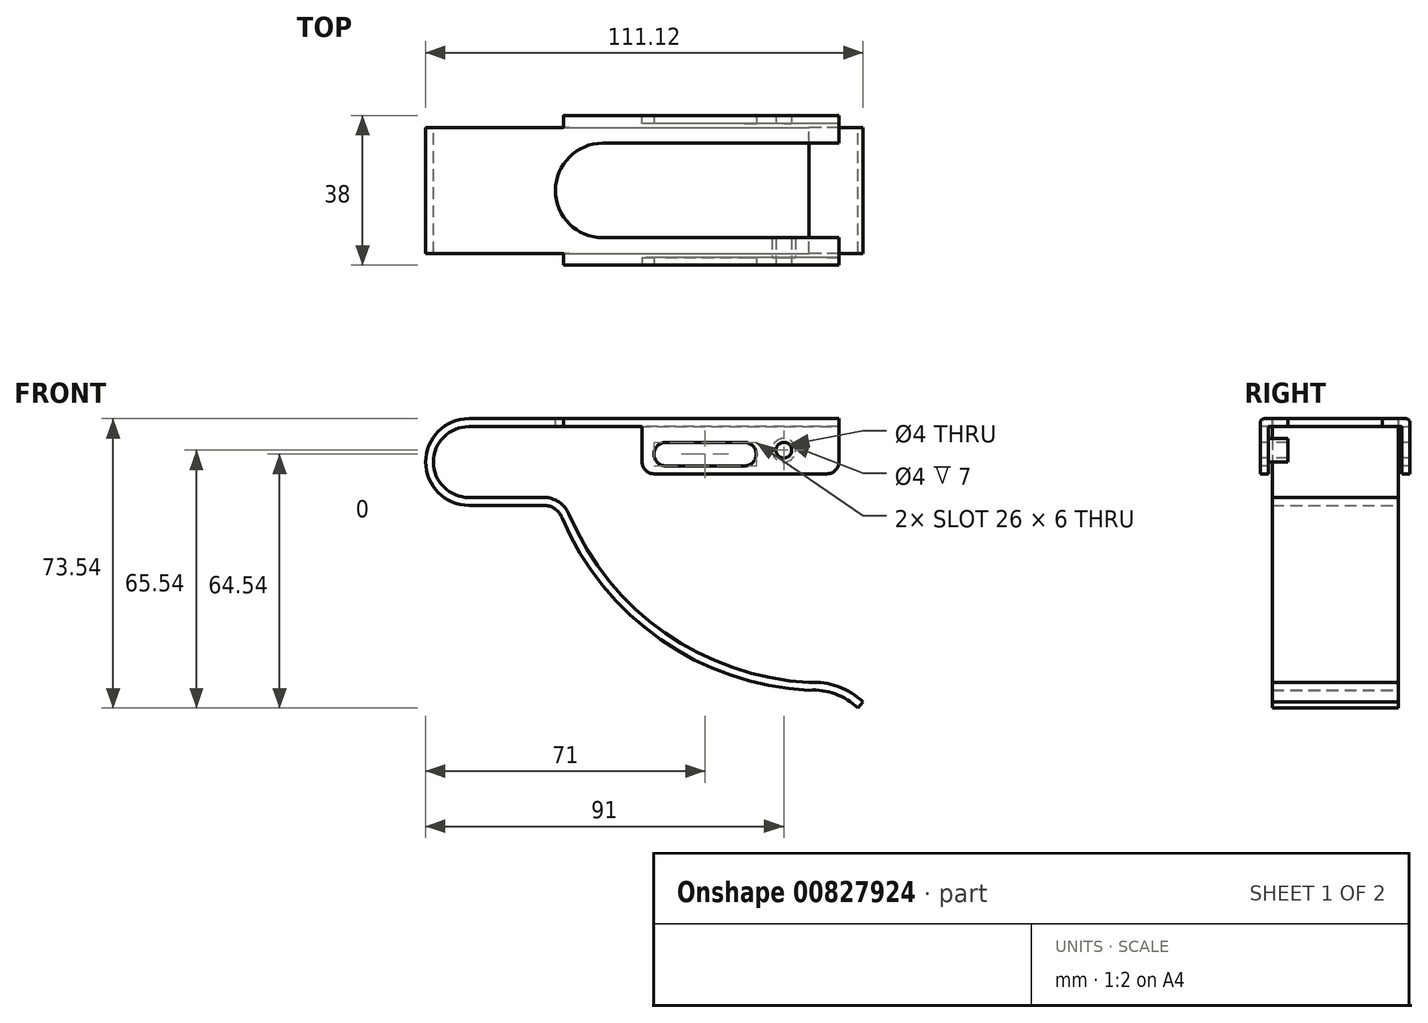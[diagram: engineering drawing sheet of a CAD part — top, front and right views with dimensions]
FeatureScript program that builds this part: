
annotation { "Feature Type Name" : "Feature", "Feature Type Description" : "" }
export const myFeature = defineFeature(function(context is Context, id is Id, definition is map)
    precondition{}
    {
        {
            var Q0;
            Q0=qCreatedBy(makeId("Front.planeOp"),FACE);
            var sketch = newSketch(context, id + "F0", { "sketchPlane" : qUnion([Q0])});
            skArc(sketch, "E0", {"start": v(0, 11) * mm, "mid": v(-11, 0) * mm, "end": v(0, -11) * mm});
            skLineSegment(sketch, "E1", {"start": v(0, 11) * mm, "end": v(94, 11) * mm});
            skLineSegment(sketch, "E2", {"start": v(0, -11) * mm, "end": v(19, -11) * mm});
            skArc(sketch, "E3", {"start": v(23.6, -14.06) * mm, "mid": v(48.7, -45.1) * mm, "end": v(86.45, -58) * mm});
            skArc(sketch, "E4", {"start": v(98.83, -62.54) * mm, "mid": v(93.13, -58.94) * mm, "end": v(86.45, -58) * mm});
            skPoint(sketch, "E5.visualSharp", {"position": v(22.4, -11) * mm});
            skArc(sketch, "E5.filletArc", {"start": v(23.6, -14.06) * mm, "mid": v(21.76, -11.83) * mm, "end": v(19, -11) * mm});
            skLineSegment(sketch, "E6.0", {"start": v(0, 9) * mm, "end": v(94, 9) * mm});
            skArc(sketch, "E6.1", {"start": v(0, 9) * mm, "mid": v(-9, 0) * mm, "end": v(0, -9) * mm});
            skArc(sketch, "E6.2", {"start": v(100.12, -61) * mm, "mid": v(93.8, -57.05) * mm, "end": v(86.43, -56) * mm});
            skArc(sketch, "E6.3", {"start": v(25.45, -13.28) * mm, "mid": v(49.79, -43.42) * mm, "end": v(86.43, -56) * mm});
            skArc(sketch, "E6.4", {"start": v(25.45, -13.28) * mm, "mid": v(22.87, -10.17) * mm, "end": v(19, -9) * mm});
            skLineSegment(sketch, "E6.5", {"start": v(0, -9) * mm, "end": v(19, -9) * mm});
            skLineSegment(sketch, "E7", {"start": v(94, 11) * mm, "end": v(94, 9) * mm});
            skLineSegment(sketch, "E8", {"start": v(100.12, -61) * mm, "end": v(98.83, -62.54) * mm});
            skLineSegment(sketch, "E9", {"start": v(100.12, -61) * mm, "end": v(153.54, -61) * mm});
            skSolve(sketch);
        }
        {
            var Q0;
            Q0=qSketchRegion(id+"F0",true);
            extrude(context, id + "F1", {"entities" : qUnion([Q0]), "depth" : 16 * mm, "offsetDistance" : 25 * mm});
        }
        {
            var Q0;
            Q0=makeQuery(id+"F1.opExtrude","SWEPT_FACE",FACE,{"disambiguationData":[OSD([sQuery(id+"F0.wireOp",EDGE,"E1")])]});
            var sketch = newSketch(context, id + "F2", { "sketchPlane" : qUnion([Q0])});
            skLineSegment(sketch, "E10.bottom", {"start": v(94, -16) * mm, "end": v(24, -16) * mm});
            skLineSegment(sketch, "E10.top", {"start": v(94, -19) * mm, "end": v(24, -19) * mm});
            skLineSegment(sketch, "E10.left", {"start": v(94, -16) * mm, "end": v(94, -19) * mm});
            skLineSegment(sketch, "E10.right", {"start": v(24, -16) * mm, "end": v(24, -19) * mm});
            skSolve(sketch);
        }
        {
            var Q0;
            Q0=makeQuery(id+"F2.imprint","IMPRINT",FACE,{"disambiguationData":[TD([[makeQuery(id+"F2.imprint","IMPRINT",EDGE,{"derivedFrom":sQuery(id+"F2.wireOp",EDGE,"E10.bottom")}),-1.0]])]});
            extrude(context, id + "F3", {"entities" : qUnion([Q0]), "operationType" : NewBodyOperationType.ADD, "oppositeDirection" : true, "depth" : 2 * mm, "offsetDistance" : 25 * mm});
        }
        {
            var Q0;
            Q0=makeQuery(id+"F3.opExtrude","SWEPT_FACE",FACE,{"disambiguationData":[OSD([sQuery(id+"F2.wireOp",EDGE,"E10.top")])]});
            var sketch = newSketch(context, id + "F4", { "sketchPlane" : qUnion([Q0])});
            skLineSegment(sketch, "E11.bottom", {"start": v(94, 11) * mm, "end": v(44, 11) * mm});
            skLineSegment(sketch, "E11.top", {"start": v(94, -3) * mm, "end": v(44, -3) * mm});
            skLineSegment(sketch, "E11.left", {"start": v(94, 11) * mm, "end": v(94, -3) * mm});
            skLineSegment(sketch, "E11.right", {"start": v(44, 11) * mm, "end": v(44, -3) * mm});
            skSolve(sketch);
        }
        {
            var Q0;
            {var subQ0=sQuery(id+"F4.wireOp",EDGE,"E11.top");Q0=makeQuery(id+"F4.imprint","IMPRINT",FACE,{"disambiguationData":[TD([[makeQuery(id+"F4.imprint","IMPRINT",EDGE,{"derivedFrom":subQ0}),-1.0]])]});}
            extrude(context, id + "F5", {"entities" : qUnion([Q0]), "operationType" : NewBodyOperationType.ADD, "oppositeDirection" : true, "depth" : 2 * mm, "offsetDistance" : 25 * mm});
        }
        {
            var Q0;
            Q0=makeQuery(id+"F3.opExtrude","CAP_EDGE",EDGE,{"disambiguationData":[OSD([sQuery(id+"F2.wireOp",EDGE,"E10.top")])],"isStart":true});
            var Q1;
            Q1=makeQuery(id+"F5.opExtrude","CAP_EDGE",EDGE,{"disambiguationData":[OSD([sQuery(id+"F2.wireOp",EDGE,"E10.top")])],"isStart":false});
            fillet(context, id + "F6", {"entities" : qUnion([Q0, Q1]), "radius" : 1 * mm, "allowEdgeOverflow" : false});
        }
        {
            var Q0;
            Q0=makeQuery(id+"F1.opExtrude","SWEPT_BODY",BODY,{"disambiguationData":[OSD([sQuery(id+"F0.wireOp",EDGE,"E0"),sQuery(id+"F0.wireOp",EDGE,"E1"),sQuery(id+"F0.wireOp",EDGE,"E2"),sQuery(id+"F0.wireOp",EDGE,"E3"),sQuery(id+"F0.wireOp",EDGE,"E4"),sQuery(id+"F0.wireOp",EDGE,"E5.filletArc"),sQuery(id+"F0.wireOp",EDGE,"E6.0"),sQuery(id+"F0.wireOp",EDGE,"E6.1"),sQuery(id+"F0.wireOp",EDGE,"E6.2"),sQuery(id+"F0.wireOp",EDGE,"E6.3"),sQuery(id+"F0.wireOp",EDGE,"E6.4"),sQuery(id+"F0.wireOp",EDGE,"E6.5"),sQuery(id+"F0.wireOp",EDGE,"E7"),sQuery(id+"F0.wireOp",EDGE,"E8")])]});
            var Q1;
            Q1=qCreatedBy(makeId("Front.planeOp"),FACE);
            mirror(context, id + "F7", {"operationType" : NewBodyOperationType.ADD, "entities" : qUnion([Q0]), "mirrorPlane" : qUnion([Q1])});
        }
        {
            var Q0;
            {var subQ0=makeQuery(id+"F3.boolean.opBoolean","MERGE",FACE,{"derivedFrom":[makeQuery(id+"F1.opExtrude","SWEPT_FACE",FACE,{"disambiguationData":[OSD([sQuery(id+"F0.wireOp",EDGE,"E1")])]}),makeQuery(id+"F3.opExtrude","CAP_FACE",FACE,{"disambiguationData":[OSD([sQuery(id+"F2.wireOp",EDGE,"E10.bottom"),sQuery(id+"F2.wireOp",EDGE,"E10.top"),sQuery(id+"F2.wireOp",EDGE,"E10.left"),sQuery(id+"F2.wireOp",EDGE,"E10.right")])],"isStart":true})]});Q0=makeQuery(id+"F7.boolean.opBoolean","MERGE",FACE,{"derivedFrom":[subQ0,makeQuery(id+"F7.opPattern","COPY",FACE,{"derivedFrom":subQ0,"instanceName":"1"})]});}
            var sketch = newSketch(context, id + "F8", { "sketchPlane" : qUnion([Q0])});
            skLineSegment(sketch, "E12", {"start": v(34, 12) * mm, "end": v(94, 12) * mm});
            skLineSegment(sketch, "E13", {"start": v(34, -12) * mm, "end": v(94, -12) * mm});
            skLineSegment(sketch, "E14", {"start": v(94, -12) * mm, "end": v(94, 12) * mm});
            skPoint(sketch, "E15.center.orphan", {"position": v(34, 0) * mm});
            skArc(sketch, "E16", {"start": v(34, 12) * mm, "mid": v(22, 0) * mm, "end": v(34, -12) * mm});
            skSolve(sketch);
        }
        {
            var Q0;
            Q0=qSketchRegion(id+"F8",true);
            extrude(context, id + "F9", {"entities" : qUnion([Q0]), "operationType" : NewBodyOperationType.REMOVE, "oppositeDirection" : true, "depth" : 2 * mm, "offsetDistance" : 25 * mm});
        }
        {
            var Q0;
            {var subQ0=sQuery(id+"F2.wireOp",EDGE,"E10.top");Q0=makeQuery(id+"F5.boolean.opBoolean","MERGE",FACE,{"derivedFrom":[makeQuery(id+"F3.opExtrude","SWEPT_FACE",FACE,{"disambiguationData":[OSD([subQ0])]}),makeQuery(id+"F5.opExtrude","CAP_FACE",FACE,{"disambiguationData":[OSD([subQ0,sQuery(id+"F4.wireOp",EDGE,"E11.top"),sQuery(id+"F4.wireOp",EDGE,"E11.left"),sQuery(id+"F4.wireOp",EDGE,"E11.right")])],"isStart":true})]});}
            var sketch = newSketch(context, id + "F10", { "sketchPlane" : qUnion([Q0])});
            skLineSegment(sketch, "E17", {"start": v(50, 2) * mm, "end": v(70, 2) * mm});
            skLineSegment(sketch, "E18.0", {"start": v(50, -1) * mm, "end": v(70, -1) * mm});
            skLineSegment(sketch, "E19.0", {"start": v(50, 5) * mm, "end": v(70, 5) * mm});
            skArc(sketch, "E20", {"start": v(50, 5) * mm, "mid": v(47, 2) * mm, "end": v(50, -1) * mm});
            skArc(sketch, "E21", {"start": v(70, -1) * mm, "mid": v(73, 2) * mm, "end": v(70, 5) * mm});
            skSolve(sketch);
        }
        {
            var Q0;
            Q0=qSketchRegion(id+"F10",true);
            extrude(context, id + "F11", {"entities" : qUnion([Q0]), "operationType" : NewBodyOperationType.REMOVE, "endBound" : BoundingType.THROUGH_ALL, "oppositeDirection" : true, "depth" : 25 * mm, "offsetDistance" : 25 * mm});
        }
        {
            var Q0;
            {var subQ0=sQuery(id+"F2.wireOp",EDGE,"E10.top");Q0=makeQuery(id+"F5.boolean.opBoolean","MERGE",FACE,{"derivedFrom":[makeQuery(id+"F3.opExtrude","SWEPT_FACE",FACE,{"disambiguationData":[OSD([subQ0])]}),makeQuery(id+"F5.opExtrude","CAP_FACE",FACE,{"disambiguationData":[OSD([subQ0,sQuery(id+"F4.wireOp",EDGE,"E11.top"),sQuery(id+"F4.wireOp",EDGE,"E11.left"),sQuery(id+"F4.wireOp",EDGE,"E11.right")])],"isStart":true})]});}
            var sketch = newSketch(context, id + "F12", { "sketchPlane" : qUnion([Q0])});
            skPoint(sketch, "E22", {"position": v(80, 3) * mm});
            skSolve(sketch);
        }
        {
            var Q0;
            Q0=sQuery(id+"F12.wireOp",VERTEX,"E22");
            var Q1;
            Q1=makeQuery(id+"F1.opExtrude","SWEPT_BODY",BODY,{"disambiguationData":[OSD([sQuery(id+"F0.wireOp",EDGE,"E0"),sQuery(id+"F0.wireOp",EDGE,"E1"),sQuery(id+"F0.wireOp",EDGE,"E2"),sQuery(id+"F0.wireOp",EDGE,"E3"),sQuery(id+"F0.wireOp",EDGE,"E4"),sQuery(id+"F0.wireOp",EDGE,"E5.filletArc"),sQuery(id+"F0.wireOp",EDGE,"E6.0"),sQuery(id+"F0.wireOp",EDGE,"E6.1"),sQuery(id+"F0.wireOp",EDGE,"E6.2"),sQuery(id+"F0.wireOp",EDGE,"E6.3"),sQuery(id+"F0.wireOp",EDGE,"E6.4"),sQuery(id+"F0.wireOp",EDGE,"E6.5"),sQuery(id+"F0.wireOp",EDGE,"E7"),sQuery(id+"F0.wireOp",EDGE,"E8")])]});
            hole(context, id + "F13", {"style" : HoleStyle.SIMPLE, "endStyle" : HoleEndStyle.THROUGH, "holeDiameter" : 4 * mm, "majorDiameter" : 5 * mm, "isTappedThrough" : true, "tappedDepth" : 12 * mm, "tapClearance" : 3, "locations" : qUnion([Q0]), "scope" : qUnion([Q1])});
        }
        {
            var Q0;
            Q0=makeQuery(id+"F5.opExtrude","CAP_FACE",FACE,{"disambiguationData":[OSD([sQuery(id+"F2.wireOp",EDGE,"E10.top"),sQuery(id+"F4.wireOp",EDGE,"E11.top"),sQuery(id+"F4.wireOp",EDGE,"E11.left"),sQuery(id+"F4.wireOp",EDGE,"E11.right")])],"isStart":false});
            var sketch = newSketch(context, id + "F14", { "sketchPlane" : qUnion([Q0])});
            skCircle(sketch, "E23.0", {"center": v(-80, 3) * mm, "radius": 2 * mm});
            skCircle(sketch, "E24.0", {"center": v(-80, 3) * mm, "radius": 3 * mm});
            skSolve(sketch);
        }
        {
            var Q0;
            Q0=qSketchRegion(id+"F14",true);
            extrude(context, id + "F15", {"entities" : qUnion([Q0]), "operationType" : NewBodyOperationType.ADD, "depth" : 5 * mm, "offsetDistance" : 25 * mm});
        }
        {
            var Q0;
            Q0=makeQuery(id+"F7.opPattern","COPY",EDGE,{"derivedFrom":makeQuery(id+"F5.opExtrude","SWEPT_EDGE",EDGE,{"disambiguationData":[OSD([sQuery(id+"F4.wireOp",EDGE,"E11.top"),sQuery(id+"F4.wireOp",EDGE,"E11.left")])]}),"instanceName":"1"});
            var Q1;
            Q1=makeQuery(id+"F7.opPattern","COPY",EDGE,{"derivedFrom":makeQuery(id+"F5.opExtrude","SWEPT_EDGE",EDGE,{"disambiguationData":[OSD([sQuery(id+"F4.wireOp",EDGE,"E11.top"),sQuery(id+"F4.wireOp",EDGE,"E11.right")])]}),"instanceName":"1"});
            var Q2;
            Q2=makeQuery(id+"F5.opExtrude","SWEPT_EDGE",EDGE,{"disambiguationData":[OSD([sQuery(id+"F4.wireOp",EDGE,"E11.top"),sQuery(id+"F4.wireOp",EDGE,"E11.right")])]});
            var Q3;
            Q3=makeQuery(id+"F5.opExtrude","SWEPT_EDGE",EDGE,{"disambiguationData":[OSD([sQuery(id+"F4.wireOp",EDGE,"E11.top"),sQuery(id+"F4.wireOp",EDGE,"E11.left")])]});
            fillet(context, id + "F16", {"entities" : qUnion([Q0, Q1, Q2, Q3]), "radius" : 3 * mm, "tangentPropagation" : true, "allowEdgeOverflow" : false});
        }
    });
